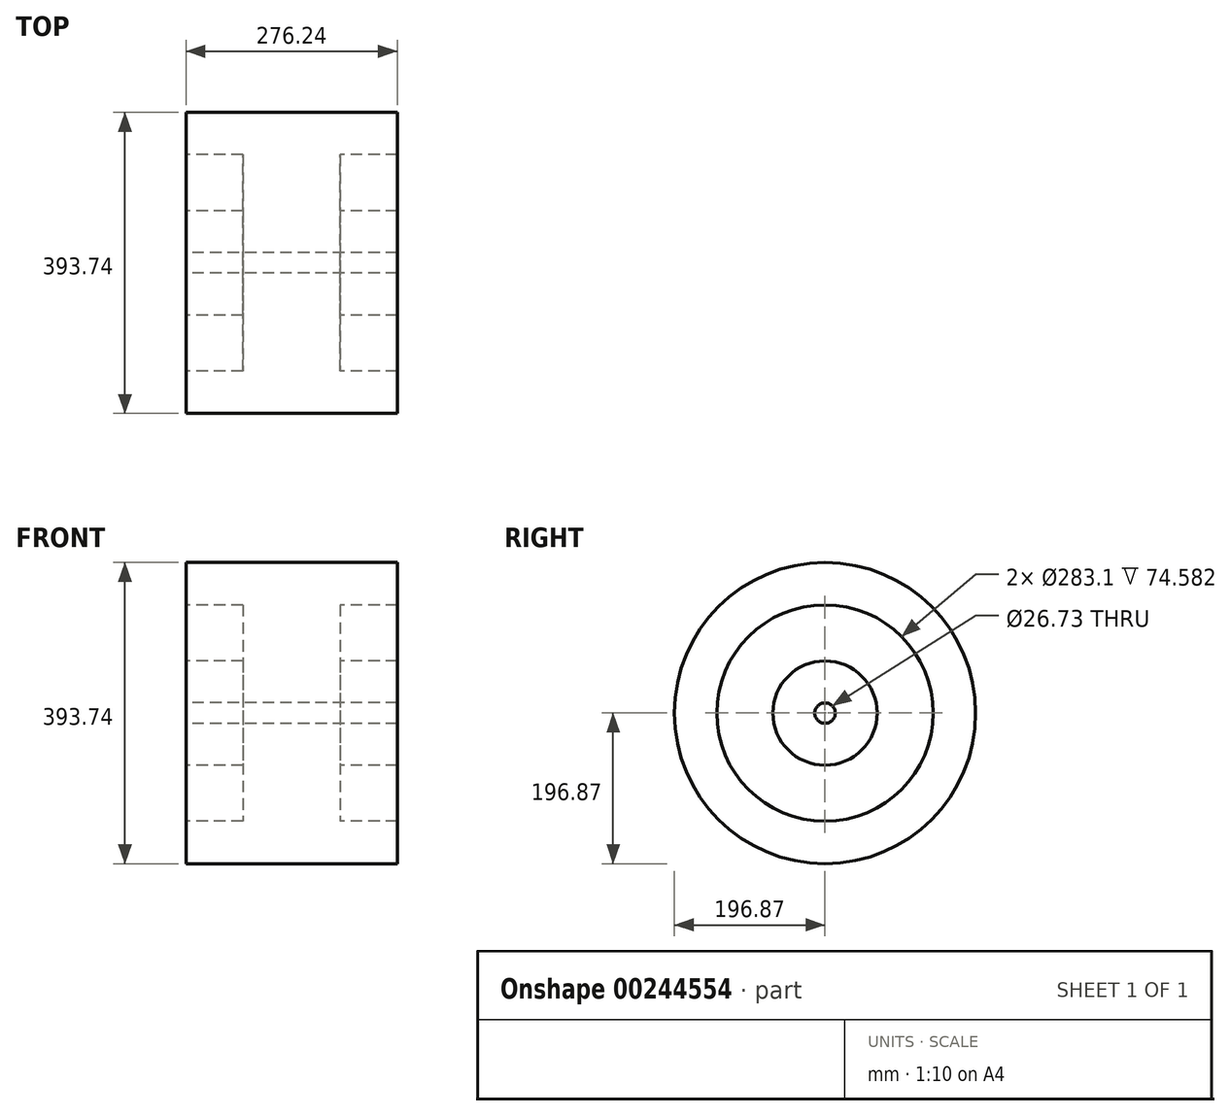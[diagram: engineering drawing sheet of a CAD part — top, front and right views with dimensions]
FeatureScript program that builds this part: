
annotation { "Feature Type Name" : "Feature", "Feature Type Description" : "" }
export const myFeature = defineFeature(function(context is Context, id is Id, definition is map)
    precondition{}
    {
        {
            var Q0;
            Q0=qCreatedBy(makeId("Front.planeOp"),FACE);
            var sketch = newSketch(context, id + "F0", { "sketchPlane" : qUnion([Q0])});
            skLineSegment(sketch, "E0", {"start": v(-117.07, 0) * mm, "end": v(128.51, 0) * mm, "construction": true});
            skLineSegment(sketch, "E1", {"start": v(-138.12, 196.87) * mm, "end": v(-138.12, 141.55) * mm});
            skLineSegment(sketch, "E2", {"start": v(-138.12, 196.87) * mm, "end": v(138.12, 196.87) * mm});
            skLineSegment(sketch, "E3", {"start": v(138.12, 196.87) * mm, "end": v(138.12, 141.55) * mm});
            skLineSegment(sketch, "E4", {"start": v(138.12, 141.55) * mm, "end": v(63.54, 141.55) * mm});
            skLineSegment(sketch, "E5", {"start": v(63.54, 141.55) * mm, "end": v(63.54, 68.2) * mm});
            skLineSegment(sketch, "E6", {"start": v(63.54, 68.2) * mm, "end": v(138.12, 68.2) * mm});
            skLineSegment(sketch, "E7", {"start": v(-138.12, 68.2) * mm, "end": v(-63.54, 68.2) * mm});
            skLineSegment(sketch, "E8", {"start": v(-63.54, 68.2) * mm, "end": v(-63.54, 141.55) * mm});
            skLineSegment(sketch, "E9", {"start": v(-63.54, 141.55) * mm, "end": v(-138.12, 141.55) * mm});
            skLineSegment(sketch, "E10", {"start": v(0, 0) * mm, "end": v(0, 214.25) * mm, "construction": true});
            skLineSegment(sketch, "E11", {"start": v(-138.12, 68.2) * mm, "end": v(-138.12, 13.37) * mm});
            skLineSegment(sketch, "E12", {"start": v(-138.12, 13.37) * mm, "end": v(138.12, 13.37) * mm});
            skLineSegment(sketch, "E13", {"start": v(138.12, 13.37) * mm, "end": v(138.12, 68.2) * mm});
            skSolve(sketch);
        }
        {
            var Q0;
            Q0 = qSketchRegion(id + "F0", true);
            var Q1;
            Q1=sQuery(id+"F0.wireOp",EDGE,"E0");
            revolve(context, id + "F1", {"entities" : qUnion([Q0]), "axis" : qUnion([Q1]), "revolveType" : RevolveType.FULL});
        }
    });
